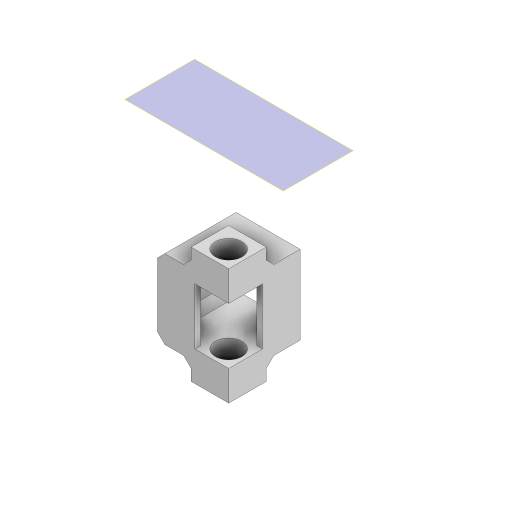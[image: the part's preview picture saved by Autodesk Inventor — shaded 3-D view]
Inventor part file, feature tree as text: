
AUTODESK INVENTOR PART (.ipt)
format: ipt  version: 2024.1 (Build 281209000, 209)  size: 185,856 bytes
history: native  units: mm
features: extrude x5, sketch x5, projected_geometry x4, other x2, plane x1, chamfer x1
ambient origin geometry x8: Origin, YZ Plane, XZ Plane, XY Plane, X Axis, Y Axis, Z Axis, Center Point
bodies: Volumenkörper1 (feature_tree)
feature tree (18):
  plane  "Arbeitsebene1"
  extrude  "Extrusion1"  Depth=19.0mm
  extrude  "Extrusion2"  Depth=19.0mm
  extrude  "Extrusion3"  Depth=3.0mm TaperAngle=0.0deg
  extrude  "Extrusion4"  Depth=3.0mm TaperAngle=0.0deg
  extrude  "Extrusion5"  Depth=9.0mm
  chamfer  "Fasen1"  Distance=9.0mm
  sketch  "Skizze1"  dims[d0=7.1mm d1=19.0mm]
  sketch  "Skizze2"  dims[d2=19.0mm d3=4.5mm]
  projected_geometry  "Projizierte Kontur1"
  sketch  "Skizze3"  dims[d4=4.5mm d5=3.0mm d6=0.0mm]
  projected_geometry  "Projizierte Kontur2"
  sketch  "Skizze4"  dims[d8=15.0mm d9=0.0mm d10=3.0mm d11=0.0mm]
  projected_geometry  "Projizierte Kontur3"
  sketch  "Skizze5"  dims[d13=1.5mm d14=9.0mm d15=9.0mm d16=10.0mm d17=10.0mm d18=5.0mm d19=0.0mm d20=10.0mm d21=10.0mm d22=5.0mm d23=0.0mm d24=2.0mm d25=2.0mm d26=45.0deg]
  projected_geometry  "Projizierte Kontur4"
  other  "Assembly_HoliSheet_v6.iam"
  other  "10_Wellplate_base_v6:1"
